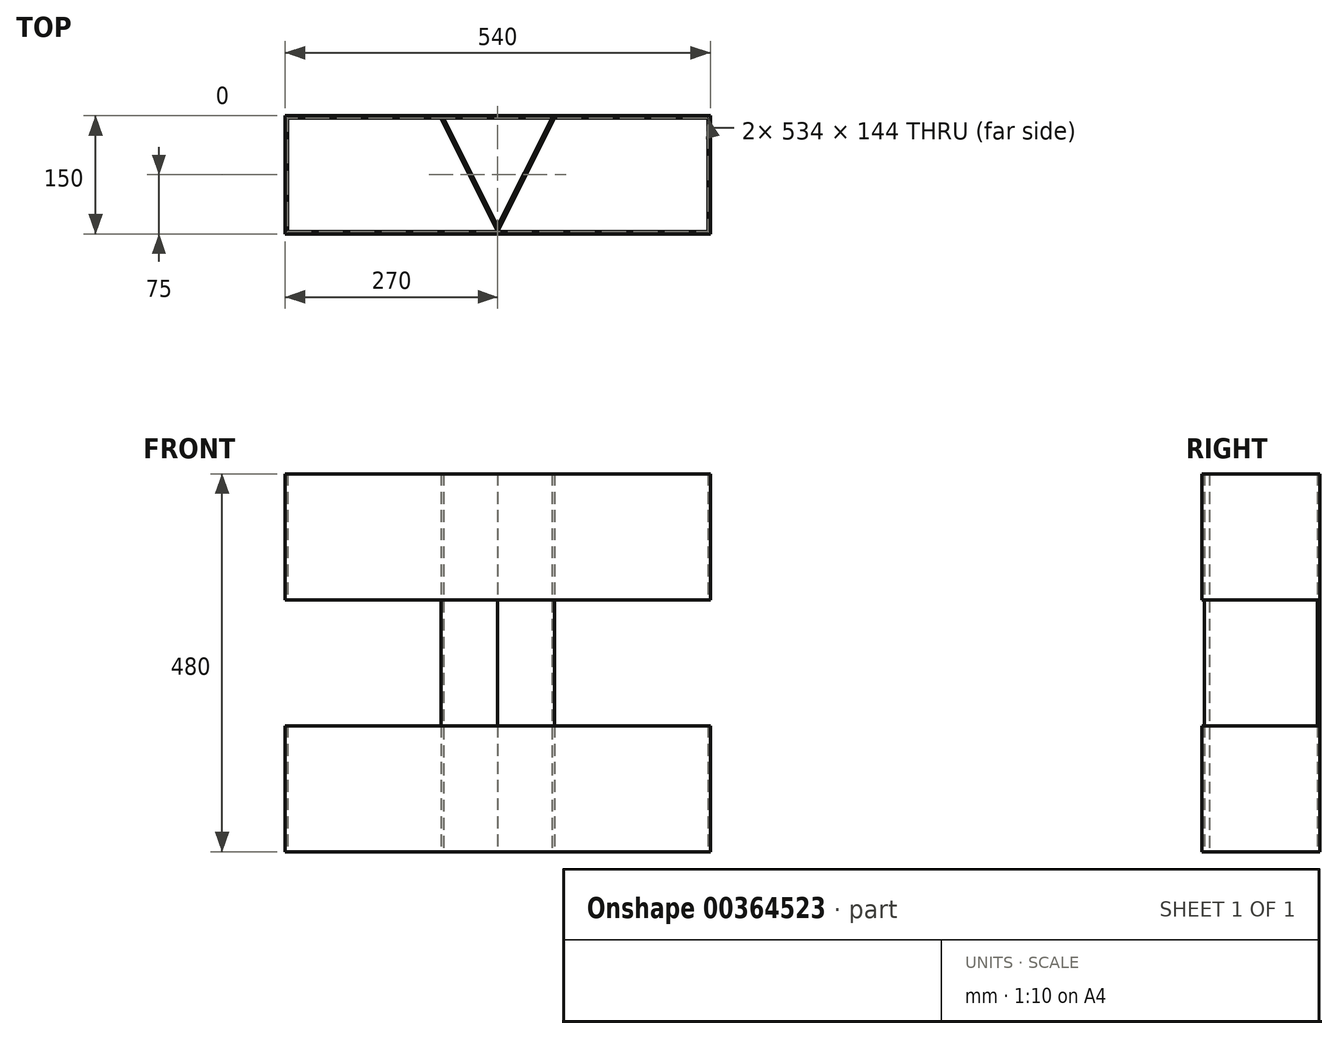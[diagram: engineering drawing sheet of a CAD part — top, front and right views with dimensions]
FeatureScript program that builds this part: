
annotation { "Feature Type Name" : "Feature", "Feature Type Description" : "" }
export const myFeature = defineFeature(function(context is Context, id is Id, definition is map)
    precondition{}
    {
        {
            var Q0;
            Q0=qCreatedBy(makeId("Top.planeOp"),FACE);
            var sketch = newSketch(context, id + "F0", { "sketchPlane" : qUnion([Q0])});
            skLineSegment(sketch, "E0.bottom", {"start": v(-270, 75) * mm, "end": v(270, 75) * mm});
            skLineSegment(sketch, "E0.top", {"start": v(-270, -75) * mm, "end": v(270, -75) * mm});
            skLineSegment(sketch, "E0.left", {"start": v(-270, 75) * mm, "end": v(-270, -75) * mm});
            skLineSegment(sketch, "E0.right", {"start": v(270, 75) * mm, "end": v(270, -75) * mm});
            skPoint(sketch, "E0.middle", {"position": v(0, 0) * mm});
            skLineSegment(sketch, "E1.0", {"start": v(-267, -72) * mm, "end": v(267, -72) * mm});
            skLineSegment(sketch, "E1.1", {"start": v(-267, 72) * mm, "end": v(-267, -72) * mm});
            skLineSegment(sketch, "E1.2", {"start": v(-267, 72) * mm, "end": v(267, 72) * mm});
            skLineSegment(sketch, "E1.3", {"start": v(267, 72) * mm, "end": v(267, -72) * mm});
            skSolve(sketch);
        }
        {
            var Q0;
            Q0=makeQuery(id+"F0.imprint","IMPRINT",FACE,{"disambiguationData":[TD([[makeQuery(id+"F0.imprint","IMPRINT",EDGE,{"derivedFrom":sQuery(id+"F0.wireOp",EDGE,"E0.bottom")}),-1.0]])]});
            extrude(context, id + "F1", {"entities" : qUnion([Q0]), "depth" : 480 * mm});
        }
        {
            var Q0;
            Q0=makeQuery(id+"F1.opExtrude","SWEPT_FACE",FACE,{"disambiguationData":[OSD([sQuery(id+"F0.wireOp",EDGE,"E0.bottom")])]});
            var sketch = newSketch(context, id + "F2", { "sketchPlane" : qUnion([Q0])});
            skLineSegment(sketch, "E2", {"start": v(-270, 240) * mm, "end": v(270, 240) * mm, "construction": true});
            skPoint(sketch, "E3.middle", {"position": v(0, 240) * mm});
            skLineSegment(sketch, "E4.bottom", {"start": v(-339.37, 320) * mm, "end": v(339.37, 320) * mm});
            skLineSegment(sketch, "E4.top", {"start": v(-339.37, 160) * mm, "end": v(339.37, 160) * mm});
            skLineSegment(sketch, "E4.left", {"start": v(-339.37, 320) * mm, "end": v(-339.37, 160) * mm});
            skLineSegment(sketch, "E4.right", {"start": v(339.37, 320) * mm, "end": v(339.37, 160) * mm});
            skSolve(sketch);
        }
        {
            var Q0;
            {var subQ0=sQuery(id+"F2.wireOp",EDGE,"E4.bottom");var subQ1=sQuery(id+"F0.wireOp",EDGE,"E0.bottom");var subQ2=makeQuery(id+"F1.opExtrude","SWEPT_EDGE",EDGE,{"disambiguationData":[OSD([subQ1,sQuery(id+"F0.wireOp",EDGE,"E0.right")])]});var subQ3=makeQuery(id+"F2.imprint","INTERSECT",VERTEX,{"derivedFrom":[subQ2,subQ0]});Q0=makeQuery(id+"F2.imprint","IMPRINT",FACE,{"disambiguationData":[TD([[makeQuery(id+"F2.imprint","IMPRINT",EDGE,{"disambiguationData":[TD([[subQ3,-1.0]])],"derivedFrom":subQ0}),-1.0]])]});}
            extrude(context, id + "F3", {"entities" : qUnion([Q0]), "operationType" : NewBodyOperationType.REMOVE, "endBound" : BoundingType.THROUGH_ALL, "oppositeDirection" : true, "depth" : 25 * mm});
        }
        {
            var Q0;
            Q0=qCreatedBy(makeId("Top.planeOp"),FACE);
            var sketch = newSketch(context, id + "F4", { "sketchPlane" : qUnion([Q0])});
            skLineSegment(sketch, "E5", {"start": v(0, -71.88) * mm, "end": v(0, 71.82) * mm, "construction": true});
            skLineSegment(sketch, "E6.bottom", {"start": v(72, 72) * mm, "end": v(68.65, 72) * mm, "construction": true});
            skLineSegment(sketch, "E6.top", {"start": v(72, -72) * mm, "end": v(-72, -72) * mm, "construction": true});
            skLineSegment(sketch, "E6.left", {"start": v(72, 72) * mm, "end": v(72, -72) * mm, "construction": true});
            skLineSegment(sketch, "E6.right", {"start": v(-72, 72) * mm, "end": v(-72, -72) * mm, "construction": true});
            skPoint(sketch, "E6.middle", {"position": v(0, 0) * mm});
            skLineSegment(sketch, "E7", {"start": v(0, -71.88) * mm, "end": v(72, 72) * mm});
            skLineSegment(sketch, "E8", {"start": v(0, -71.88) * mm, "end": v(-72, 72) * mm});
            skLineSegment(sketch, "E9", {"start": v(72, 72) * mm, "end": v(-72, 72) * mm});
            skLineSegment(sketch, "E10.trimOffspring", {"start": v(0, -65.18) * mm, "end": v(-68.65, 72) * mm});
            skLineSegment(sketch, "E11.trimOffspring", {"start": v(0, -65.18) * mm, "end": v(68.65, 72) * mm});
            skLineSegment(sketch, "E12.trimOffspring", {"start": v(-68.65, 72) * mm, "end": v(-72, 72) * mm, "construction": true});
            skSolve(sketch);
        }
        {
            var Q0;
            {var subQ3=sQuery(id+"F4.wireOp",EDGE,"E7");Q0=makeQuery(id+"F4.imprint","IMPRINT",FACE,{"disambiguationData":[TD([[makeQuery(id+"F4.imprint","IMPRINT",EDGE,{"derivedFrom":subQ3}),1.0]])]});}
            extrude(context, id + "F5", {"entities" : qUnion([Q0]), "depth" : 480 * mm});
        }
        {
            var Q0;
            {var subQ2=sQuery(id+"F0.wireOp",EDGE,"E0.bottom");Q0=makeQuery(id+"F3.boolean.opBoolean","SPLIT",FACE,{"disambiguationData":[TD([makeQuery(id+"F3.opExtrude","SWEPT_FACE",FACE,{"disambiguationData":[OSD([sQuery(id+"F2.wireOp",EDGE,"E4.bottom")])]})])],"derivedFrom":makeQuery(id+"F1.opExtrude","SWEPT_FACE",FACE,{"disambiguationData":[OSD([subQ2])]})});}
            var sketch = newSketch(context, id + "F6", { "sketchPlane" : qUnion([Q0])});
            skLineSegment(sketch, "E13.bottom", {"start": v(-72, 320) * mm, "end": v(72, 320) * mm});
            skLineSegment(sketch, "E13.top", {"start": v(-72, 160) * mm, "end": v(72, 160) * mm});
            skLineSegment(sketch, "E13.left", {"start": v(-72, 320) * mm, "end": v(-72, 160) * mm});
            skLineSegment(sketch, "E13.right", {"start": v(72, 320) * mm, "end": v(72, 160) * mm});
            skSolve(sketch);
        }
        {
            var Q0;
            Q0=makeQuery(id+"F6.imprint","IMPRINT",FACE,{"disambiguationData":[TD([[makeQuery(id+"F6.imprint","IMPRINT",EDGE,{"derivedFrom":sQuery(id+"F6.wireOp",EDGE,"E13.bottom")}),-1.0]])]});
            extrude(context, id + "F7", {"entities" : qUnion([Q0]), "oppositeDirection" : true, "depth" : 3 * mm});
        }
    });
